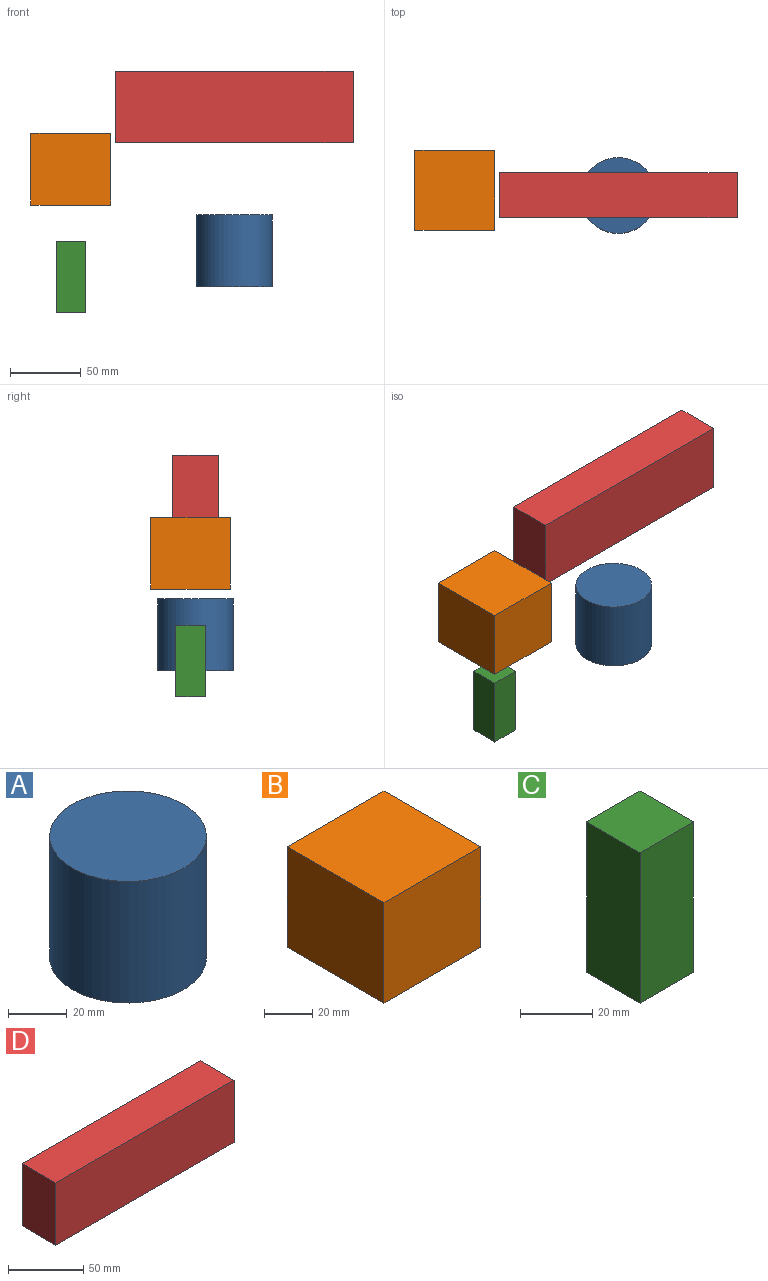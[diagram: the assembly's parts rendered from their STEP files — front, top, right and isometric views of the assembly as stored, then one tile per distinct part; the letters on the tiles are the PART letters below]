
ASSEMBLY  parts=4 mates=2
PART A: 3 faces, bbox 53.5x53.5x50.8 mm
  f0: cylinder r=26.77mm len=53.54mm, axis (0,0,-1), area 8544mm2, adj f1,f2
  f1: plane 53.54x53.54mm, normal (0,0,1), area 2251mm2, adj f0
  f2: plane 53.54x53.54mm, normal (0,0,-1), area 2251mm2, adj f0
PART B: 6 faces, bbox 56.4x56.4x50.8 mm
  f0: plane 56.42x50.8mm, normal (-1,0,0), area 2866.1mm2, adj f1,f3,f4,f5
  f1: plane 56.42x50.8mm, normal (0,-1,0), area 2866.1mm2, adj f0,f2,f4,f5
  f2: plane 56.42x50.8mm, normal (1,0,0), area 2866.1mm2, adj f1,f3,f4,f5
  f3: plane 56.42x50.8mm, normal (0,1,0), area 2866.1mm2, adj f0,f2,f4,f5
  f4: plane 56.42x56.42mm, normal (0,0,1), area 3183.2mm2, adj f0,f1,f2,f3
  f5: plane 56.42x56.42mm, normal (0,0,-1), area 3183.2mm2, adj f0,f1,f2,f3
PART C: 6 faces, bbox 20.8x20.8x50.8 mm
  f0: plane 50.8x20.84mm, normal (0,1,0), area 1058.6mm2, adj f1,f3,f4,f5
  f1: plane 50.8x20.84mm, normal (-1,0,0), area 1058.6mm2, adj f0,f2,f4,f5
  f2: plane 50.8x20.84mm, normal (0,-1,0), area 1058.6mm2, adj f1,f3,f4,f5
  f3: plane 50.8x20.84mm, normal (1,0,0), area 1058.6mm2, adj f0,f2,f4,f5
  f4: plane 20.84x20.84mm, normal (0,0,1), area 434.2mm2, adj f0,f1,f2,f3
  f5: plane 20.84x20.84mm, normal (0,0,-1), area 434.2mm2, adj f0,f1,f2,f3
PART D: 6 faces, bbox 167.9x31.8x50.8 mm
  f0: plane 167.88x50.8mm, normal (0,1,0), area 8528.5mm2, adj f1,f3,f4,f5
  f1: plane 50.8x31.85mm, normal (-1,0,0), area 1617.8mm2, adj f0,f2,f4,f5
  f2: plane 167.88x50.8mm, normal (0,-1,0), area 8528.5mm2, adj f1,f3,f4,f5
  f3: plane 50.8x31.85mm, normal (1,0,0), area 1617.8mm2, adj f0,f2,f4,f5
  f4: plane 167.88x31.85mm, normal (0,0,1), area 5346.5mm2, adj f0,f1,f2,f3
  f5: plane 167.88x31.85mm, normal (0,0,-1), area 5346.5mm2, adj f0,f1,f2,f3
PLACE A t=(67.22,55,27.27)mm fixed
PLACE B rot(axis=(1,0,0),180deg) t=(58.73,23.62,135.83)mm
PLACE C t=(63.94,40.82,8.83)mm
PLACE D rot(axis=(-1,0,0),180deg) t=(72.13,104.74,179.67)mm
MATE revolute D.f4 <-> A.f0  axis (0,0,-1) through (85.8,52.15,128.87)mm
MATE slider B.f4 <-> C.f4  axis (0,0,-1) through (-29.54,55.66,85.03)mm
